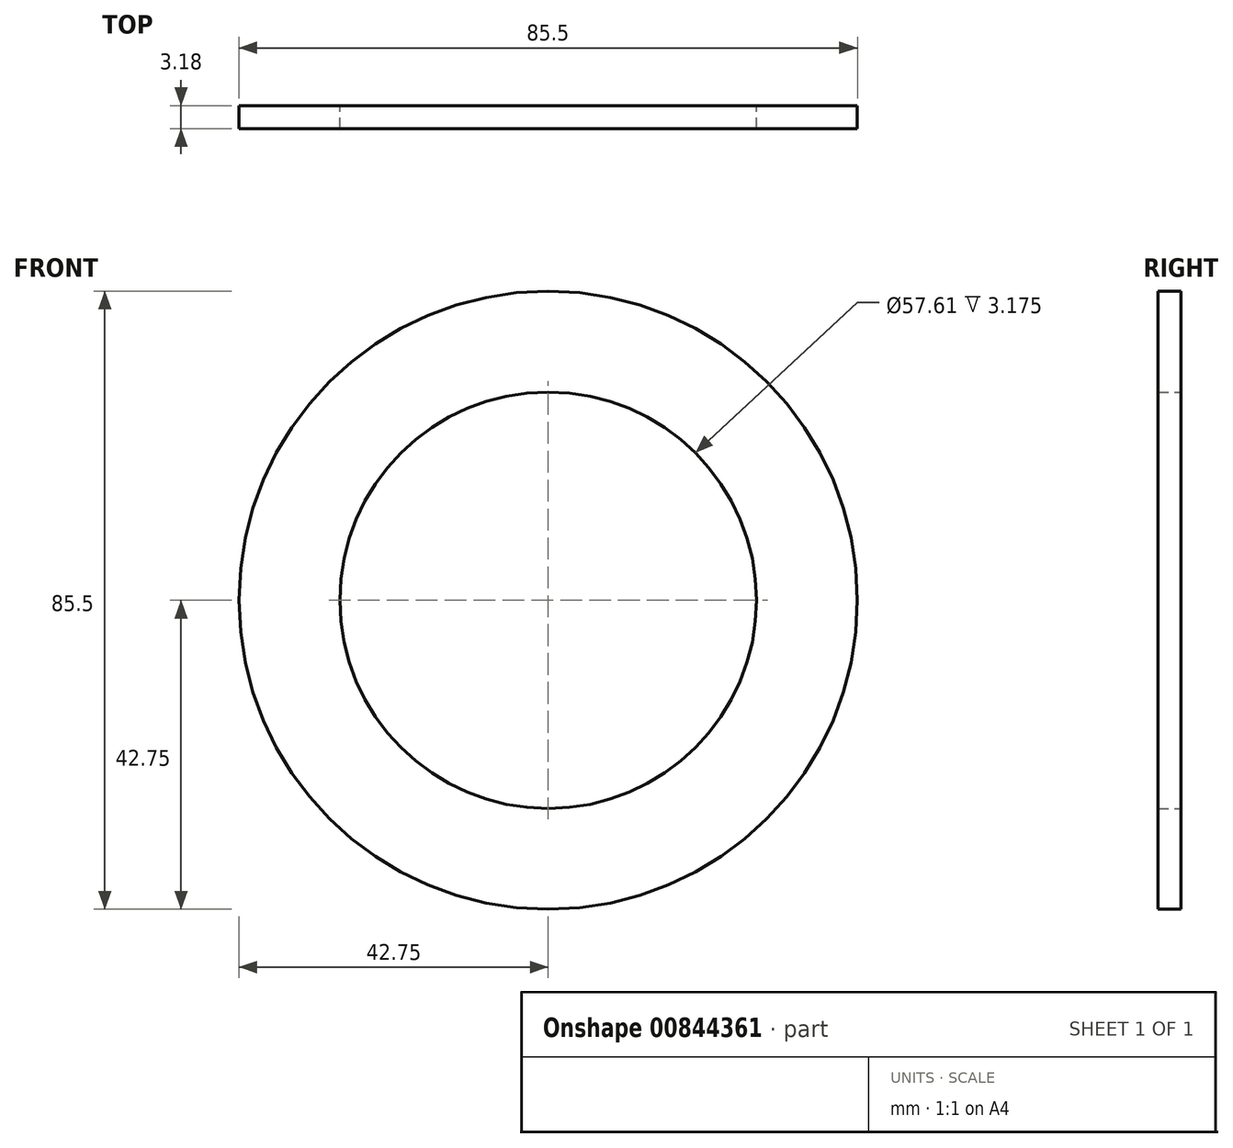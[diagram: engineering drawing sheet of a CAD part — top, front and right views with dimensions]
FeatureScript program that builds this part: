
annotation { "Feature Type Name" : "Feature", "Feature Type Description" : "" }
export const myFeature = defineFeature(function(context is Context, id is Id, definition is map)
    precondition{}
    {
        {
            var Q0;
            Q0=qCreatedBy(makeId("Front.planeOp"),FACE);
            var sketch = newSketch(context, id + "F0", { "sketchPlane" : qUnion([Q0])});
            skCircle(sketch, "E0", {"center": v(0, 0) * mm, "radius": 42.75 * mm});
            skCircle(sketch, "E1", {"center": v(0, 0) * mm, "radius": 28.8 * mm});
            skSolve(sketch);
        }
        {
            var Q0;
            Q0=makeQuery(id+"F0.imprint","IMPRINT",FACE,{"disambiguationData":[TD([[makeQuery(id+"F0.imprint","IMPRINT",EDGE,{"derivedFrom":sQuery(id+"F0.wireOp",EDGE,"E0")}),1.0]])]});
            extrude(context, id + "F1", {"entities" : qUnion([Q0]), "depth" : 3.17 * mm, "offsetDistance" : 25.4 * mm});
        }
    });
